# Revit family: Deckel_Kreuzung_Russia
name_source: partatom
category: Generic Models
revit_build: Autodesk Revit 2015 (Build: 20140606_1530(x64)
units: mm (PartAtom-declared; Revit-internal decimal feet)

## types (7) — shared parameters
Manufacturer = OBO Bettermann
Material = Steel, Galvanized
URL = http://www.obo-bettermann.com

## per-type parameters (varying)
| type | A | B | GTIN | Manufacturer Art. No. |
| DFK 100 FS RU | 200 mm  [stored 0.656168 ft] | 134 mm  [stored 0.439633 ft] | 4012196649495 | 7128750 |
| DFK 150 FS RU | 250 mm  [stored 0.82021 ft] | 184 mm  [stored 0.603675 ft] | 4012196649501 | 7128752 |
| DFK 200 FS RU | 300 mm | 234 mm  [stored 0.767717 ft] | 4012196649549 | 7128754 |
| DFK 300 FS RU | 400 mm  [stored 1.31234 ft] | 334 mm  [stored 1.0958 ft] | 4012196649556 | 7128756 |
| DFK 400 FS RU | 500 mm  [stored 1.64042 ft] | 434 mm  [stored 1.42388 ft] | 4012196649563 | 7128758 |
| DFK 500 FS RU | 600 mm | 534 mm  [stored 1.75197 ft] | 4012196649570 | 7128760 |
| DFK 600 FS RU | 700 mm  [stored 2.29659 ft] | 634 mm  [stored 2.08005 ft] | 4012196649587 | 7128762 |

note: column(s) folded — value = type name in every type: Article Type

note: [stored X ft] marks values corroborated as IEEE doubles in the binary element streams (Revit-internal decimal feet)

## geometry (parser evidence)
native form markers: Sweep x2
no freeform markers — native parametric forms only
